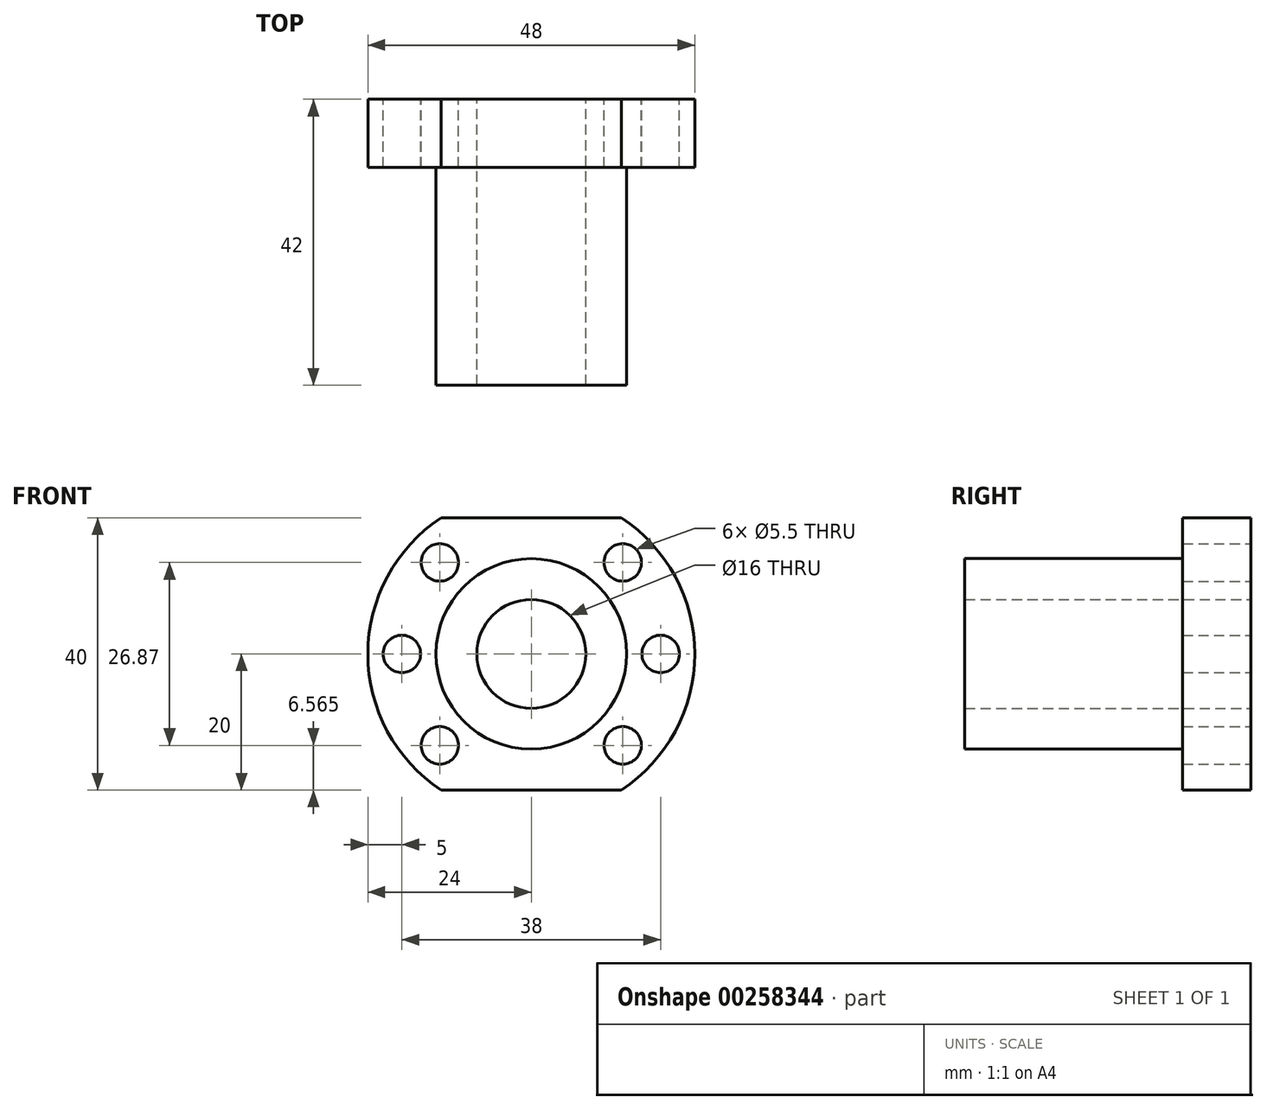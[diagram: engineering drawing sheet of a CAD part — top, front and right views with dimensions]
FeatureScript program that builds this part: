
annotation { "Feature Type Name" : "Feature", "Feature Type Description" : "" }
export const myFeature = defineFeature(function(context is Context, id is Id, definition is map)
    precondition{}
    {
        {
            var Q0;
            Q0=qCreatedBy(makeId("Front.planeOp"),FACE);
            var sketch = newSketch(context, id + "F0", { "sketchPlane" : qUnion([Q0])});
            skArc(sketch, "E0", {"start": v(-13.27, 20) * mm, "mid": v(-24, 0) * mm, "end": v(-13.27, -20) * mm});
            skLineSegment(sketch, "E1", {"start": v(13.27, 20) * mm, "end": v(-13.27, 20) * mm});
            skLineSegment(sketch, "E2", {"start": v(-13.27, -20) * mm, "end": v(13.27, -20) * mm});
            skLineSegment(sketch, "E3", {"start": v(-24, 0) * mm, "end": v(24, 0) * mm, "construction": true});
            skArc(sketch, "E4.trimOffspring", {"start": v(13.27, -20) * mm, "mid": v(24, 0) * mm, "end": v(13.27, 20) * mm});
            skCircle(sketch, "E5", {"center": v(0, 0) * mm, "radius": 19 * mm, "construction": true});
            skCircle(sketch, "E6", {"center": v(13.44, 13.44) * mm, "radius": 2.75 * mm});
            skCircle(sketch, "E7", {"center": v(19, 0) * mm, "radius": 2.75 * mm});
            skCircle(sketch, "E8", {"center": v(13.44, -13.44) * mm, "radius": 2.75 * mm});
            skCircle(sketch, "E9", {"center": v(-13.44, -13.44) * mm, "radius": 2.75 * mm});
            skCircle(sketch, "E10", {"center": v(-19, 0) * mm, "radius": 2.75 * mm});
            skCircle(sketch, "E11", {"center": v(-13.44, 13.44) * mm, "radius": 2.75 * mm});
            skLineSegment(sketch, "E12", {"start": v(0, 20) * mm, "end": v(0, -20) * mm, "construction": true});
            skLineSegment(sketch, "E13", {"start": v(-13.44, 13.44) * mm, "end": v(13.44, -13.44) * mm, "construction": true});
            skSolve(sketch);
        }
        {
            var Q0;
            Q0=qSketchRegion(id+"F0",true);
            var Q1;
            Q1=sQuery(id+"F0.wireOp",EDGE,"E13");
            extrude(context, id + "F1", {"entities" : qUnion([Q0]), "surfaceEntities" : qUnion([Q1]), "depth" : 10 * mm});
        }
        {
            var Q0;
            Q0=makeQuery(id+"F1.opExtrude","CAP_FACE",FACE,{"disambiguationData":[OSD([sQuery(id+"F0.wireOp",EDGE,"E0"),sQuery(id+"F0.wireOp",EDGE,"E1"),sQuery(id+"F0.wireOp",EDGE,"E2"),sQuery(id+"F0.wireOp",EDGE,"E4.trimOffspring"),sQuery(id+"F0.wireOp",EDGE,"E6"),sQuery(id+"F0.wireOp",EDGE,"E7"),sQuery(id+"F0.wireOp",EDGE,"E8"),sQuery(id+"F0.wireOp",EDGE,"E9"),sQuery(id+"F0.wireOp",EDGE,"E10"),sQuery(id+"F0.wireOp",EDGE,"E11")])],"isStart":false});
            var sketch = newSketch(context, id + "F2", { "sketchPlane" : qUnion([Q0])});
            skCircle(sketch, "E14", {"center": v(0, 0) * mm, "radius": 14 * mm});
            skSolve(sketch);
        }
        {
            var Q0;
            Q0=qSketchRegion(id+"F2",true);
            extrude(context, id + "F3", {"entities" : qUnion([Q0]), "operationType" : NewBodyOperationType.ADD, "depth" : 32 * mm});
        }
        {
            var Q0;
            Q0=makeQuery(id+"F1.opExtrude","CAP_FACE",FACE,{"disambiguationData":[OSD([sQuery(id+"F0.wireOp",EDGE,"E0"),sQuery(id+"F0.wireOp",EDGE,"E1"),sQuery(id+"F0.wireOp",EDGE,"E2"),sQuery(id+"F0.wireOp",EDGE,"E4.trimOffspring"),sQuery(id+"F0.wireOp",EDGE,"E6"),sQuery(id+"F0.wireOp",EDGE,"E7"),sQuery(id+"F0.wireOp",EDGE,"E8"),sQuery(id+"F0.wireOp",EDGE,"E9"),sQuery(id+"F0.wireOp",EDGE,"E10"),sQuery(id+"F0.wireOp",EDGE,"E11")])],"isStart":true});
            var sketch = newSketch(context, id + "F4", { "sketchPlane" : qUnion([Q0])});
            skCircle(sketch, "E15", {"center": v(0, 0) * mm, "radius": 8 * mm});
            skSolve(sketch);
        }
        {
            var Q0;
            Q0=qSketchRegion(id+"F4",true);
            extrude(context, id + "F5", {"entities" : qUnion([Q0]), "operationType" : NewBodyOperationType.REMOVE, "endBound" : BoundingType.UP_TO_NEXT, "oppositeDirection" : true, "depth" : 25 * mm});
        }
    });
